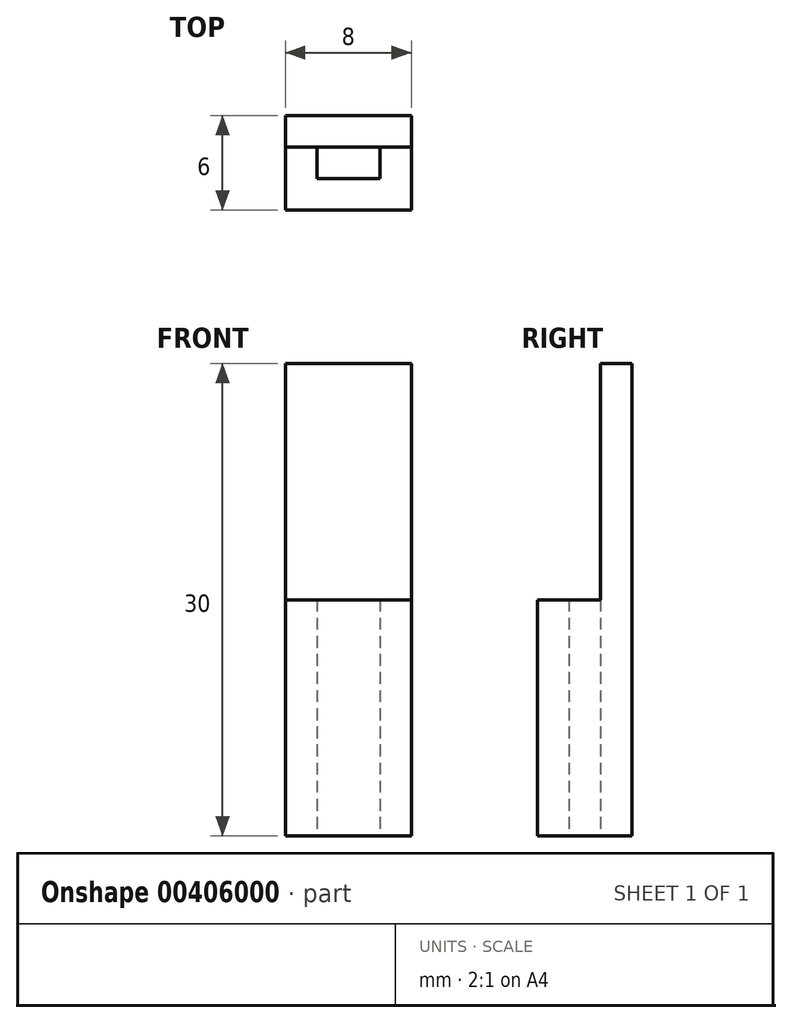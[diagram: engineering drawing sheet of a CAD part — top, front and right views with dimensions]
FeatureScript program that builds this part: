
annotation { "Feature Type Name" : "Feature", "Feature Type Description" : "" }
export const myFeature = defineFeature(function(context is Context, id is Id, definition is map)
    precondition{}
    {
        {
            var Q0;
            Q0=qCreatedBy(makeId("Top.planeOp"),FACE);
            var sketch = newSketch(context, id + "F0", { "sketchPlane" : qUnion([Q0])});
            skLineSegment(sketch, "E0.bottom", {"start": v(2, 1) * mm, "end": v(-2, 1) * mm});
            skLineSegment(sketch, "E0.top", {"start": v(2, -1) * mm, "end": v(-2, -1) * mm});
            skLineSegment(sketch, "E0.left", {"start": v(2, 1) * mm, "end": v(2, -1) * mm});
            skLineSegment(sketch, "E0.right", {"start": v(-2, 1) * mm, "end": v(-2, -1) * mm});
            skPoint(sketch, "E0.middle", {"position": v(0, 0) * mm});
            skLineSegment(sketch, "E1.0", {"start": v(4, 3) * mm, "end": v(-4, 3) * mm});
            skLineSegment(sketch, "E1.1", {"start": v(4, 3) * mm, "end": v(4, -3) * mm});
            skLineSegment(sketch, "E1.2", {"start": v(4, -3) * mm, "end": v(-4, -3) * mm});
            skLineSegment(sketch, "E1.3", {"start": v(-4, 3) * mm, "end": v(-4, -3) * mm});
            skSolve(sketch);
        }
        {
            var Q0;
            Q0=makeQuery(id+"F0.imprint","IMPRINT",FACE,{"disambiguationData":[TD([[makeQuery(id+"F0.imprint","IMPRINT",EDGE,{"derivedFrom":sQuery(id+"F0.wireOp",EDGE,"E0.bottom")}),-1.0]])]});
            extrude(context, id + "F1", {"entities" : qUnion([Q0]), "depth" : 15 * mm});
        }
        {
            var Q0;
            Q0=makeQuery(id+"F1.opExtrude","CAP_FACE",FACE,{"disambiguationData":[OSD([sQuery(id+"F0.wireOp",EDGE,"E0.bottom"),sQuery(id+"F0.wireOp",EDGE,"E0.top"),sQuery(id+"F0.wireOp",EDGE,"E0.left"),sQuery(id+"F0.wireOp",EDGE,"E0.right"),sQuery(id+"F0.wireOp",EDGE,"E1.0"),sQuery(id+"F0.wireOp",EDGE,"E1.1"),sQuery(id+"F0.wireOp",EDGE,"E1.2"),sQuery(id+"F0.wireOp",EDGE,"E1.3")])],"isStart":false});
            var sketch = newSketch(context, id + "F2", { "sketchPlane" : qUnion([Q0])});
            skLineSegment(sketch, "E2.bottom", {"start": v(-4, 1) * mm, "end": v(4, 1) * mm});
            skLineSegment(sketch, "E2.top", {"start": v(-4, 3) * mm, "end": v(4, 3) * mm});
            skLineSegment(sketch, "E2.left", {"start": v(-4, 1) * mm, "end": v(-4, 3) * mm});
            skLineSegment(sketch, "E2.right", {"start": v(4, 1) * mm, "end": v(4, 3) * mm});
            skSolve(sketch);
        }
        {
            var Q0;
            Q0 = qSketchRegion(id + "F2", true);
            extrude(context, id + "F3", {"entities" : qUnion([Q0]), "operationType" : NewBodyOperationType.ADD, "depth" : 15 * mm});
        }
    });
